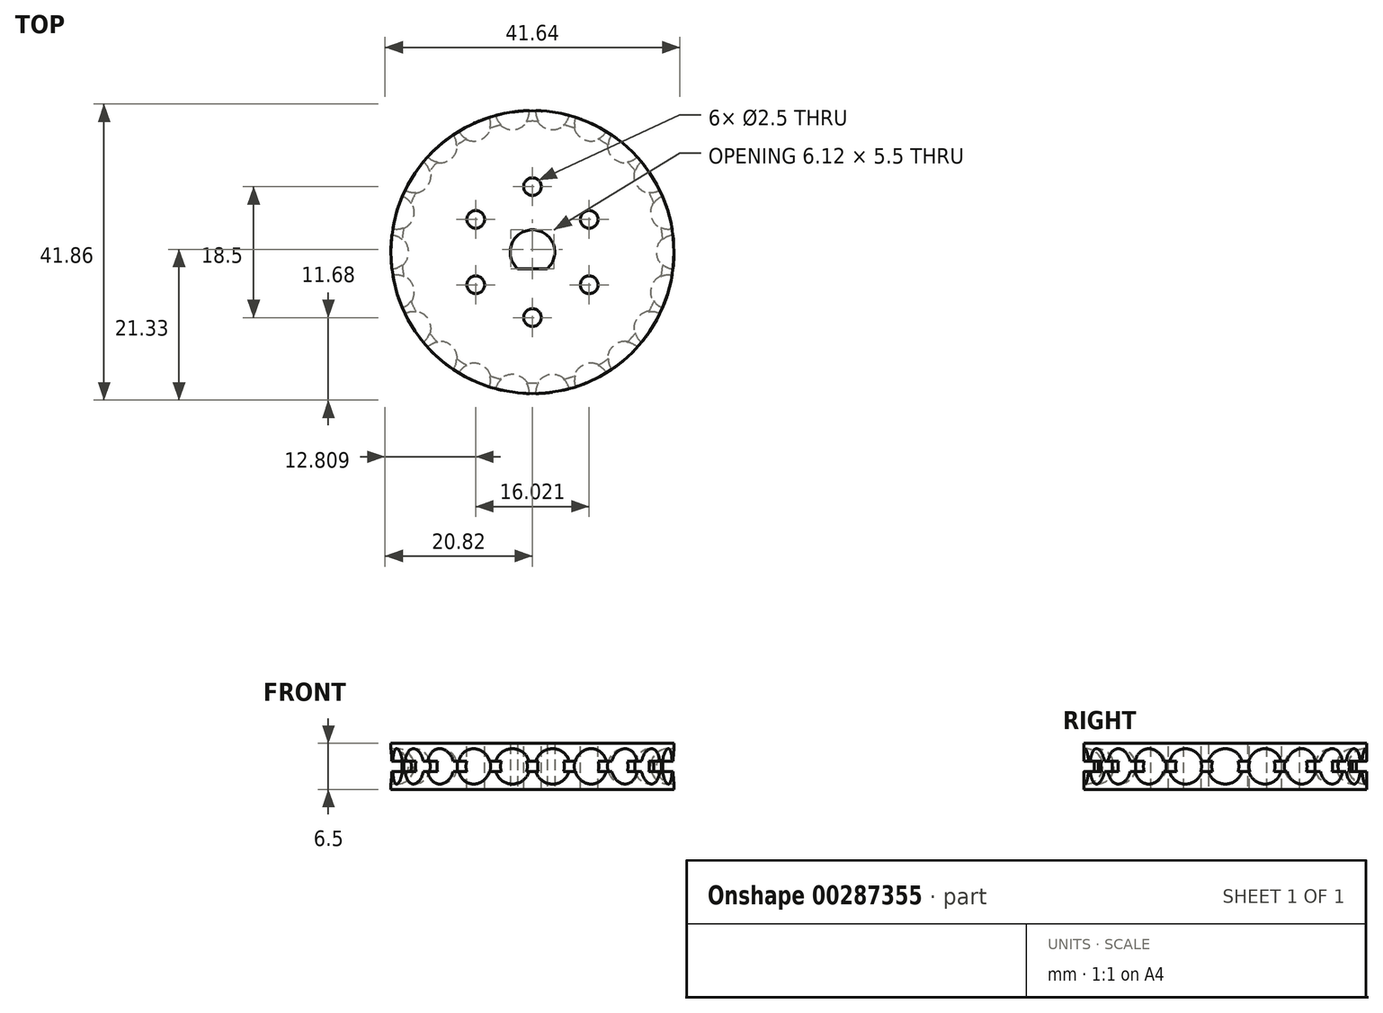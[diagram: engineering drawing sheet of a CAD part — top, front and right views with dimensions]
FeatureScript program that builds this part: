
annotation { "Feature Type Name" : "Feature", "Feature Type Description" : "" }
export const myFeature = defineFeature(function(context is Context, id is Id, definition is map)
    precondition{}
    {
        {
            assignVariable(context, id + "F0", {"name" : "diameter", "anyValue" : 40});
        }
        {
            var Q0;
            Q0=qCreatedBy(makeId("Top.planeOp"),FACE);
            var sketch = newSketch(context, id + "F1", { "sketchPlane" : qUnion([Q0])});
            skCircle(sketch, "E0", {"center": v(0, 0) * mm, "radius": 20 * mm});
            skSolve(sketch);
        }
        {
            var Q0;
            Q0 = qSketchRegion(id + "F1", true);
            extrude(context, id + "F2", {"entities" : qUnion([Q0]), "depth" : 6.5 * mm});
        }
        {
            var Q0;
            Q0=qCreatedBy(makeId("Right.planeOp"),FACE);
            cPlane(context, id + "F3", {"entities" : qUnion([Q0]), "cplaneType" : CPlaneType.OFFSET, "offset" : (getVariable(context, 'diameter') / 2) * mm, "width" : 152.4 * mm, "height" : 152.4 * mm});
        }
        {
            var Q0;
            Q0=qCreatedBy(id+"F3.planeOp",FACE);
            var sketch = newSketch(context, id + "F4", { "sketchPlane" : qUnion([Q0])});
            skArc(sketch, "E1", {"start": v(0, 5.75) * mm, "mid": v(-2.5, 3.25) * mm, "end": v(0, 0.75) * mm});
            skLineSegment(sketch, "E2", {"start": v(0, 5.75) * mm, "end": v(0, 0.75) * mm});
            skLineSegment(sketch, "E3", {"start": v(0, 0) * mm, "end": v(0, 0.75) * mm, "construction": true});
            skLineSegment(sketch, "E4", {"start": v(0, 6.5) * mm, "end": v(0, 5.75) * mm, "construction": true});
            skSolve(sketch);
        }
        {
            var Q0;
            Q0 = qSketchRegion(id + "F4", true);
            var Q1;
            Q1=sQuery(id+"F4.wireOp",EDGE,"E2");
            revolve(context, id + "F5", {"entities" : qUnion([Q0]), "axis" : qUnion([Q1]), "revolveType" : RevolveType.FULL, "oppositeDirection" : true});
        }
        {
            var Q0;
            Q0=makeQuery(id+"F5.opRevolve","SWEPT_BODY",BODY,{"disambiguationData":[OSD([sQuery(id+"F4.wireOp",EDGE,"E1"),sQuery(id+"F4.wireOp",EDGE,"E2")])]});
            var Q1;
            Q1=makeQuery(id+"F2.opExtrude","CAP_EDGE",EDGE,{"disambiguationData":[OSD([sQuery(id+"F1.wireOp",EDGE,"E0")])],"isStart":true});
            circularPattern(context, id + "F6", {"operationType" : NewBodyOperationType.REMOVE, "entities" : qUnion([Q0]), "axis" : qUnion([Q1]), "angle" : 360 * degree, "instanceCount" : 22, "equalSpace" : true});
        }
        {
            var Q0;
            Q0=qCreatedBy(makeId("Top.planeOp"),FACE);
            var sketch = newSketch(context, id + "F7", { "sketchPlane" : qUnion([Q0])});
            skArc(sketch, "E5", {"start": v(2.1, -2.35) * mm, "mid": v(0, 3.15) * mm, "end": v(-2.1, -2.35) * mm});
            skLineSegment(sketch, "E6", {"start": v(0, 3.15) * mm, "end": v(0, -2.35) * mm, "construction": true});
            skLineSegment(sketch, "E7", {"start": v(2.1, -2.35) * mm, "end": v(-2.1, -2.35) * mm});
            skSolve(sketch);
        }
        {
            var Q0;
            Q0 = qSketchRegion(id + "F7", true);
            extrude(context, id + "F8", {"entities" : qUnion([Q0]), "operationType" : NewBodyOperationType.REMOVE, "endBound" : BoundingType.UP_TO_NEXT, "depth" : 25.4 * mm});
        }
        {
            var Q0;
            Q0=qCreatedBy(makeId("Front.planeOp"),FACE);
            var sketch = newSketch(context, id + "F9", { "sketchPlane" : qUnion([Q0])});
            skLineSegment(sketch, "E8", {"start": v(-20, 0) * mm, "end": v(-20, 2.5) * mm, "construction": true});
            skLineSegment(sketch, "E9", {"start": v(-20, 3.25) * mm, "end": v(0, 3.25) * mm, "construction": true});
            skLineSegment(sketch, "E10", {"start": v(-20, 4) * mm, "end": v(-18.5, 4) * mm});
            skLineSegment(sketch, "E11", {"start": v(-18.5, 4) * mm, "end": v(-18.5, 2.5) * mm});
            skLineSegment(sketch, "E12", {"start": v(-18.5, 2.5) * mm, "end": v(-20, 2.5) * mm});
            skLineSegment(sketch, "E13", {"start": v(-20, 2.5) * mm, "end": v(-20, 4) * mm});
            skLineSegment(sketch, "E14", {"start": v(-20, 4) * mm, "end": v(-20, 3.25) * mm});
            skLineSegment(sketch, "E15.trimOffspring", {"start": v(-20, 4) * mm, "end": v(-20, 6.5) * mm, "construction": true});
            skLineSegment(sketch, "E16", {"start": v(-20, 2.5) * mm, "end": v(-20, 3.25) * mm});
            skSolve(sketch);
        }
        {
            var Q0;
            Q0=makeQuery(id+"F9.imprint","IMPRINT",FACE,{"disambiguationData":[TD([[makeQuery(id+"F9.imprint","IMPRINT",EDGE,{"derivedFrom":sQuery(id+"F9.wireOp",EDGE,"E10")}),-1.0]])]});
            var Q1;
            Q1=makeQuery(id+"F2.opExtrude","CAP_EDGE",EDGE,{"disambiguationData":[OSD([sQuery(id+"F1.wireOp",EDGE,"E0")])],"isStart":true});
            revolve(context, id + "F10", {"operationType" : NewBodyOperationType.REMOVE, "entities" : qUnion([Q0]), "axis" : qUnion([Q1]), "revolveType" : RevolveType.FULL, "oppositeDirection" : true});
        }
        {
            var Q0;
            Q0=makeQuery(id+"F2.opExtrude","CAP_FACE",FACE,{"disambiguationData":[OSD([sQuery(id+"F1.wireOp",EDGE,"E0")])],"isStart":false});
            var sketch = newSketch(context, id + "F11", { "sketchPlane" : qUnion([Q0])});
            skPoint(sketch, "E17", {"position": v(0, 9.25) * mm});
            skPoint(sketch, "E18.1.0", {"position": v(-8.01, 4.63) * mm});
            skPoint(sketch, "E18.2.0", {"position": v(-8.01, -4.62) * mm});
            skPoint(sketch, "E18.3.0", {"position": v(0, -9.25) * mm});
            skPoint(sketch, "E18.4.0", {"position": v(8.01, -4.63) * mm});
            skPoint(sketch, "E18.5.0", {"position": v(8.01, 4.63) * mm});
            skPoint(sketch, "E18.center", {"position": v(0, 0) * mm});
            skSolve(sketch);
        }
        {
            var Q0;
            Q0=sQuery(id+"F11.wireOp",VERTEX,"E18.5.0");
            var Q1;
            Q1=sQuery(id+"F11.wireOp",VERTEX,"E17");
            var Q2;
            Q2=sQuery(id+"F11.wireOp",VERTEX,"E18.1.0");
            var Q3;
            Q3=sQuery(id+"F11.wireOp",VERTEX,"E18.2.0");
            var Q4;
            Q4=sQuery(id+"F11.wireOp",VERTEX,"E18.3.0");
            var Q5;
            Q5=sQuery(id+"F11.wireOp",VERTEX,"E18.4.0");
            var Q6;
            Q6=makeQuery(id+"F2.opExtrude","SWEPT_BODY",BODY,{"disambiguationData":[OSD([sQuery(id+"F1.wireOp",EDGE,"E0")])]});
            hole(context, id + "F12", {"style" : HoleStyle.SIMPLE, "endStyle" : HoleEndStyle.THROUGH, "holeDiameter" : 2.5 * mm, "majorDiameter" : 5 * mm, "tappedDepth" : 12.7 * mm, "tapClearance" : 3, "locations" : qUnion([Q0, Q1, Q2, Q3, Q4, Q5]), "scope" : qUnion([Q6])});
        }
    });
